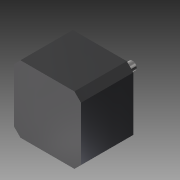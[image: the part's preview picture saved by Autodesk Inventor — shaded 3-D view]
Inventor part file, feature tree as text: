
AUTODESK INVENTOR PART (.ipt)
format: ipt  version: 2013 (Build 170138000, 138)  size: 134,656 bytes
history: native  units: mm
features: thread x4, sketch x4, extrude x3, hole x1
ambient origin geometry x8: Origin, YZ Plane, XZ Plane, XY Plane, X Axis, Y Axis, Z Axis, Center Point
bodies: Solid1 (feature_tree)
feature tree (12):
  extrude  "Extrusion1"  Depth=41.0mm
  extrude  "Extrusion4"  Depth=20.5mm
  extrude  "Extrusion5"  Depth=4.0mm
  hole  "Hole1"  [1 undecoded]
  thread  "Thread1"  [1 undecoded]
  thread  "Thread2"  [1 undecoded]
  thread  "Thread3"  [1 undecoded]
  thread  "Thread4"  [1 undecoded]
  sketch  "Sketch1"  dims[d0=41.0mm d2=41.0mm]
  sketch  "Sketch4"  dims[d3=20.5mm d4=20.5mm]
  sketch  "Sketch5"  dims[d5=4.0mm d6=4.0mm]
  sketch  "Sketch6"  dims[d7=4.0mm d8=4.0mm d9=4.0mm d10=4.0mm d11=4.0mm d12=4.0mm d13=32.0mm d14=0.0mm d24=23.0mm d26=9.5mm d27=2.0mm d28=0.0mm d29=5.0mm d31=20.0mm d32=0.0mm d33=15.5mm d34=15.5mm d35=20.0mm d37=31.0mm d38=20.0mm d40=31.0mm d43=2.5mm d44=6.0mm d45=4.0mm d46=2.0mm d47=90.0deg d48=8.0mm d49=20.594885mm d50=10.0mm d51=0.0mm d52=10.0mm d53=0.0mm d54=10.0mm d55=0.0mm d56=10.0mm d57=0.0mm]
note: 5 required parameter values undecoded (feature->parameter linkage not recoverable at this tier; creation-order binding heuristic only, values carry confidence <= 0.55)
